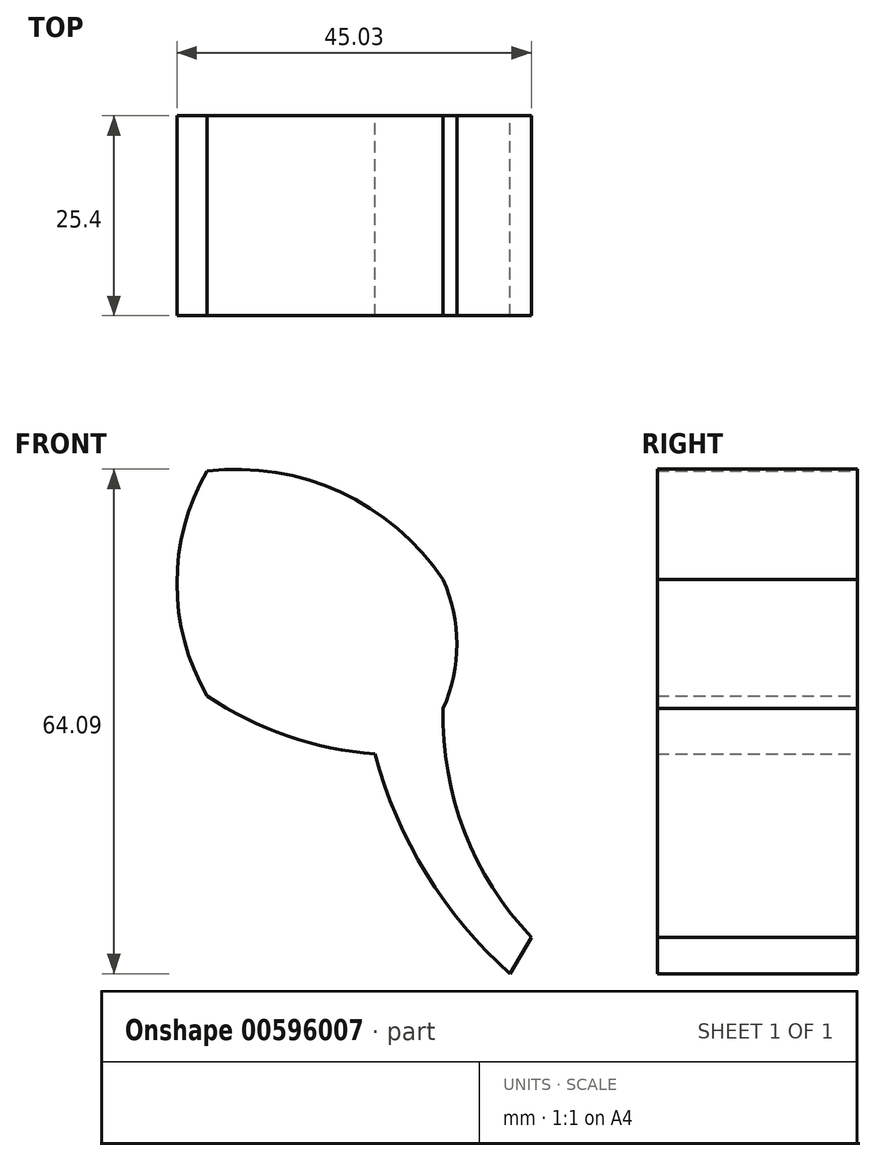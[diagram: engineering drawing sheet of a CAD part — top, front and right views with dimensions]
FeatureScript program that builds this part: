
annotation { "Feature Type Name" : "Feature", "Feature Type Description" : "" }
export const myFeature = defineFeature(function(context is Context, id is Id, definition is map)
    precondition{}
    {
        {
            var Q0;
            Q0=qCreatedBy(makeId("Front.planeOp"),FACE);
            var sketch = newSketch(context, id + "F0", { "sketchPlane" : qUnion([Q0])});
            skArc(sketch, "E0", {"start": v(30, -13.82) * mm, "mid": v(16.94, -2.7) * mm, "end": v(0, 0) * mm});
            skArc(sketch, "E1", {"start": v(30, -30.19) * mm, "mid": v(31.72, -22) * mm, "end": v(30, -13.82) * mm});
            skArc(sketch, "E2", {"start": v(30, -30.19) * mm, "mid": v(32.7, -45.84) * mm, "end": v(41.2, -59.27) * mm});
            skLineSegment(sketch, "E3", {"start": v(41.2, -59.27) * mm, "end": v(38.46, -63.88) * mm});
            skArc(sketch, "E4", {"start": v(21.34, -35.98) * mm, "mid": v(27.86, -51.18) * mm, "end": v(38.46, -63.88) * mm});
            skArc(sketch, "E5", {"start": v(0, -28.58) * mm, "mid": v(10.2, -33.66) * mm, "end": v(21.34, -35.98) * mm});
            skArc(sketch, "E6", {"start": v(0, 0) * mm, "mid": v(-3.83, -14.3) * mm, "end": v(0, -28.58) * mm});
            skSolve(sketch);
        }
        {
            var Q0;
            Q0=makeQuery(id+"F0.imprint","IMPRINT",FACE,{"disambiguationData":[TD([[makeQuery(id+"F0.imprint","IMPRINT",EDGE,{"derivedFrom":sQuery(id+"F0.wireOp",EDGE,"E0")}),1.0]])]});
            extrude(context, id + "F1", {"entities" : qUnion([Q0]), "endBound" : BoundingType.SYMMETRIC, "depth" : 25.4 * mm, "offsetDistance" : 25.4 * mm});
        }
    });
